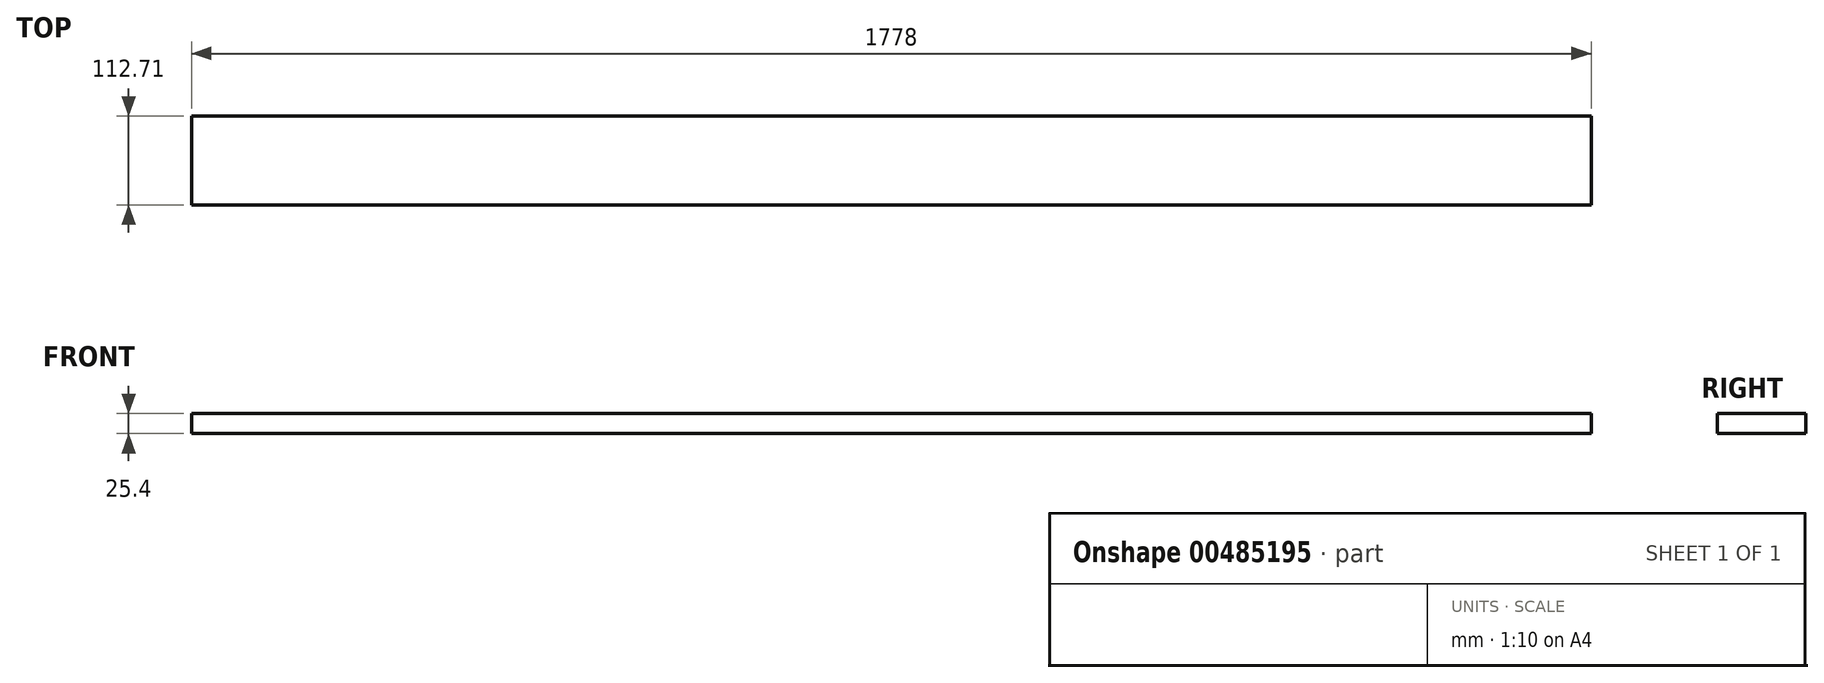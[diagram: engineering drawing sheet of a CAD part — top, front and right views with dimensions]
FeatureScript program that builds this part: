
annotation { "Feature Type Name" : "Feature", "Feature Type Description" : "" }
export const myFeature = defineFeature(function(context is Context, id is Id, definition is map)
    precondition{}
    {
        {
            var Q0;
            Q0=qCreatedBy(makeId("Front.planeOp"),FACE);
            var sketch = newSketch(context, id + "F0", { "sketchPlane" : qUnion([Q0])});
            skLineSegment(sketch, "E0.bottom", {"start": v(0, 0) * mm, "end": v(1778, 0) * mm});
            skLineSegment(sketch, "E0.top", {"start": v(0, -25.4) * mm, "end": v(1778, -25.4) * mm});
            skLineSegment(sketch, "E0.left", {"start": v(0, 0) * mm, "end": v(0, -25.4) * mm});
            skLineSegment(sketch, "E0.right", {"start": v(1778, 0) * mm, "end": v(1778, -25.4) * mm});
            skSolve(sketch);
        }
        {
            var Q0;
            Q0 = qSketchRegion(id + "F0", true);
            extrude(context, id + "F1", {"entities" : qUnion([Q0]), "oppositeDirection" : true, "depth" : 112.7 * mm});
        }
    });
